FCSTD DOCUMENT  (FreeCAD 0.18.4R)
Label: container.v6
License: All rights reserved
LicenseURL: http://en.wikipedia.org/wiki/All_rights_reserved
objects: Part::Feature×11, Part::Extrusion×10, Part::Part2DObjectPython×7, Part::MultiFuse×3, Part::FeaturePython×3, App::DocumentObjectGroup×2, Part::Cut×1
note: 35 computed .brp shape members not serialized (recipe doc carries the construction recipe); baked Part::Feature solids carry a one-line shape summary decoded from their .brp

FEATURE [Part::Feature] Cut001001  label="Cut002"
  shape: bbox 73.48 x 120 x 121.6 mm, 4537 faces (baked)
FEATURE [Part::Feature] Fusion018002001008014
  Placement = pos=(63.0552,-240.375,-121.554) rot=(0,0,1;0rad)
  shape: bbox 46.3 x 120 x 5.151 mm, 1154 faces (baked)
FEATURE [Part::Part2DObjectPython] Wire  # Draft 2D object (typed FeaturePython)
  ChamferSize = 0
  Closed = true
  End = (149.94,5.9047,-131.382)
  FilletRadius = 0
  Length = 330.896
  MakeFace = true
  Placement = pos=(137.639,5.9047,-9.82831) rot=(1,0,0;1.5708rad)
  Points = (4) [(0,0,0),(-43.2967,-6.92779e-14,1.33227e-14),(-30.9437,-121.554,-2.04281e-14),(12.3006,-121.554,-1.59872e-14)]
  Start = (137.639,5.9047,-9.82831)
  Subdivisions = 0
  Support = -> [Cut001001]
FEATURE [Part::Extrusion] Extrusion
  Base = -> Wire
  Dir = (-2.55e-14,-117,3.6e-15)
  DirMode = 0
  FaceMakerClass = Part::FaceMakerBullseye
  LengthFwd = 0
  LengthRev = 0
  Solid = true
  Symmetric = false
FEATURE [Part::Cut] Cut
  Base = -> Cut001001
  Tool = -> Extrusion
FEATURE [Part::Feature] Fusion001002001  label="Fusion001003"
  shape: bbox 4.191 x 71 x 7.994 mm, 13 faces (baked)
FEATURE [Part::Feature] Face
  shape: bbox 0.8119 x 5 x 7.959 mm, 1 faces, 0 solids (baked)
FEATURE [Part::Extrusion] Extrusion001
  Base = -> Face
  Dir = (1.17358,-1.56e-14,0.119723)
  DirMode = 0
  FaceMakerClass = Part::FaceMakerBullseye
  LengthFwd = 0
  LengthRev = 0
  Solid = true
  Symmetric = false
FEATURE [Part::Feature] Face001
  shape: bbox 0.8119 x 6 x 7.959 mm, 1 faces, 0 solids (baked)
FEATURE [Part::Extrusion] Extrusion002
  Base = -> Face001
  Dir = (1.17358,-1.58e-14,0.119723)
  DirMode = 0
  FaceMakerClass = Part::FaceMakerBullseye
  LengthFwd = 0
  LengthRev = 0
  Solid = true
  Symmetric = false
FEATURE [Part::Feature] Fusion018002001008015
  Placement = pos=(6.06632,-6.985e-12,-59.6925) rot=(0,0,1;0rad)
  shape: bbox 4.191 x 71 x 7.994 mm, 13 faces (baked)
FEATURE [Part::Feature] Face002
  Placement = pos=(6.06632,-6.985e-12,-59.6925) rot=(0,0,1;0rad)
  shape: bbox 0.8119 x 6 x 7.959 mm, 1 faces, 0 solids (baked)
FEATURE [Part::Extrusion] Extrusion003
  Base = -> Face002
  Dir = (1.16236,-1.57e-14,0.118578)
  DirMode = 0
  FaceMakerClass = Part::FaceMakerBullseye
  LengthFwd = 0
  LengthRev = 0
  Solid = true
  Symmetric = false
FEATURE [Part::Feature] Face003
  Placement = pos=(6.06632,-6.985e-12,-59.6925) rot=(0,0,1;0rad)
  shape: bbox 0.8119 x 5 x 7.959 mm, 1 faces, 0 solids (baked)
FEATURE [Part::Extrusion] Extrusion004
  Base = -> Face003
  Dir = (1.16101,-1.54e-14,0.118441)
  DirMode = 0
  FaceMakerClass = Part::FaceMakerBullseye
  LengthFwd = 0
  LengthRev = 0
  Solid = true
  Symmetric = false
FEATURE [Part::Part2DObjectPython] Wire001  # Draft 2D object (typed FeaturePython)
  ChamferSize = 0
  Closed = true
  End = (147.812,-11.2487,-95.1691)
  FilletRadius = 0
  Length = 49.7972
  MakeFace = true
  Placement = pos=(148.52,-11.2487,-102.133) rot=(0,1,0;1.46952rad)
  Points = (8) [(0,0,0),(1.37849,-1.3786,0),(1.37849,-15.3786,0),(-4.26326e-14,-16.7572,0),(-6.99946,-16.7572,-2.84217e-13),(-8.37795,-15.3786,0),(-8.37795,-1.3786,0),(-6.99946,7.10543e-15,0)]
  Start = (148.52,-11.2487,-102.133)
  Subdivisions = 0
FEATURE [Part::Part2DObjectPython] Wire002  # Draft 2D object (typed FeaturePython)
  ChamferSize = 0
  Closed = true
  End = (141.767,-77.7487,-35.6862)
  FilletRadius = 0
  Length = 49.7972
  MakeFace = true
  Placement = pos=(142.475,-77.7487,-42.6498) rot=(0,1,0;1.46952rad)
  Points = (8) [(0,0,0),(1.37849,-1.3786,0),(1.37849,-15.3786,0),(-4.26326e-14,-16.7572,0),(-6.99946,-16.7572,-2.84217e-13),(-8.37795,-15.3786,0),(-8.37795,-1.3786,0),(-6.99946,0,1.7053e-13)]
  Start = (142.475,-77.7487,-42.6498)
  Subdivisions = 0
FEATURE [Part::Part2DObjectPython] Wire003  # Draft 2D object (typed FeaturePython)
  ChamferSize = 0
  Closed = true
  End = (147.812,-81.2487,-95.1691)
  FilletRadius = 0
  Length = 49.7972
  MakeFace = true
  Placement = pos=(148.52,-81.2487,-102.133) rot=(0,1,0;1.46952rad)
  Points = (8) [(0,0,0),(1.37849,-1.3786,0),(1.37849,-15.3786,0),(-4.26326e-14,-16.7572,0),(-6.99946,-16.7572,-2.84217e-13),(-8.37795,-15.3786,0),(-8.37795,-1.3786,0),(-6.99946,0,2.27374e-13)]
  Start = (148.52,-81.2487,-102.133)
  Subdivisions = 0
FEATURE [Part::Part2DObjectPython] Wire004  # Draft 2D object (typed FeaturePython)
  ChamferSize = 0
  Closed = true
  End = (141.767,-14.7487,-35.6862)
  FilletRadius = 0
  Length = 49.7972
  MakeFace = true
  Placement = pos=(142.475,-14.7487,-42.6498) rot=(0,1,0;1.46952rad)
  Points = (8) [(0,0,0),(1.37849,-1.3786,0),(1.37849,-15.3786,0),(-4.26326e-14,-16.7572,0),(-6.99946,-16.7572,-2.84217e-13),(-8.37795,-15.3786,0),(-8.37795,-1.3786,0),(-6.99946,7.10543e-15,0)]
  Start = (142.475,-14.7487,-42.6498)
  Subdivisions = 0
FEATURE [Part::Extrusion] Extrusion005
  Base = -> Wire004
  Dir = (-1.48467,5.8e-15,-0.150881)
  DirMode = 0
  FaceMakerClass = Part::FaceMakerBullseye
  LengthFwd = 0
  LengthRev = 0
  Solid = true
  Symmetric = false
FEATURE [Part::Extrusion] Extrusion006
  Base = -> Wire002
  Dir = (-1.48467,6.4e-15,-0.150881)
  DirMode = 0
  FaceMakerClass = Part::FaceMakerBullseye
  LengthFwd = 0
  LengthRev = 0
  Solid = true
  Symmetric = false
FEATURE [Part::Extrusion] Extrusion007
  Base = -> Wire003
  Dir = (-1.48467,8.6e-15,-0.150881)
  DirMode = 0
  FaceMakerClass = Part::FaceMakerBullseye
  LengthFwd = 0
  LengthRev = 0
  Solid = true
  Symmetric = false
FEATURE [Part::Extrusion] Extrusion008
  Base = -> Wire001
  Dir = (-1.48467,5.7e-15,-0.150881)
  DirMode = 0
  FaceMakerClass = Part::FaceMakerBullseye
  LengthFwd = 0
  LengthRev = 0
  Solid = true
  Symmetric = false
FEATURE [Part::MultiFuse] Fusion
  Shapes = -> [Extrusion007,Fusion018002001008015,Extrusion008,Extrusion006,Fusion001002001,Extrusion005]
FEATURE [Part::MultiFuse] Fusion018002001008016
  Shapes = -> [Fusion,Cut]
FEATURE [Part::Feature] Fusion018002001008016001  label="Fusion018002001008017"
  shape: bbox 73.48 x 120 x 121.6 mm, 4427 faces (baked)
FEATURE [Part::FeaturePython] Slice_child1  label="Slice.1"  # WARN: FeaturePython — macro-defined, semantics opaque (R4)
  FilterType = 1
  Invert = false
  OverrideMaxVal = 0
  WindowFrom = 80
  WindowTo = 100
  items = 1
FEATURE [App::DocumentObjectGroup] GrExplode_Slice  label="Exploded Slice"
  Group = -> [Slice_child1]
FEATURE [Part::Part2DObjectPython] Rectangle  # Draft 2D object (typed FeaturePython)
  ChamferSize = 0
  Columns = 1
  FilletRadius = 0
  Height = 193
  Length = 154
  MakeFace = true
  Placement = pos=(92.5503,-317.731,-183.654) rot=(1,0,0;3.14159rad)
  Rows = 1
  Support = -> [Slice_child1]
FEATURE [Part::FeaturePython] Slice  # WARN: FeaturePython — macro-defined, semantics opaque (R4)
  Base = -> Slice_child1
  Mode = 1
  Tolerance = 0
  Tools = -> [Rectangle]
FEATURE [Part::FeaturePython] Slice_child0  label="Slice.0"  # WARN: FeaturePython — macro-defined, semantics opaque (R4)
  Base = -> Slice
  FilterType = 1
  Invert = false
  OverrideMaxVal = 0
  Placement = pos=(258.315,131.738,-193.634) rot=(0,1,0;3.14159rad)
  WindowFrom = 80
  WindowTo = 100
  items = 0
FEATURE [Part::Part2DObjectPython] Wire005  # Draft 2D object (typed FeaturePython)
  ChamferSize = 0
  Closed = true
  End = (151.417,-340.152,-131.382)
  FilletRadius = 0
  Length = 8.77005
  MakeFace = true
  Placement = pos=(151.72,-340.152,-128.398) rot=(0.787614,0.60907,-0.093265;3.93915rad)
  Points = (3) [(0,0,0),(-1.74661,0.247326,3.33188),(-1.0363,1.74338,2.21059)]
  Start = (151.72,-340.152,-128.398)
  Subdivisions = 0
FEATURE [Part::Extrusion] Extrusion009
  Base = -> Wire005
  Dir = (2.78485e-11,115.318,-5.34519e-10)
  DirMode = 0
  FaceMakerClass = Part::FaceMakerBullseye
  LengthFwd = 0
  LengthRev = 0
  Solid = true
  Symmetric = false
FEATURE [Part::MultiFuse] Fusion018002001008016002
  Shapes = -> [Extrusion009,Slice_child0]
FEATURE [App::DocumentObjectGroup] GrExplode_Slice001  label="Exploded Slice001"
  Group = -> [Fusion018002001008016002]
FEATURE [Part::Feature] Fusion018002001008016002_solid  label="Fusion018002001008016002 (Solid)"
  shape: bbox 73.97 x 118.7 x 121.4 mm, 508 faces (baked)
FEATURE [Part::Feature] Fusion018002001008016003
  Placement = pos=(52.9375,-470.393,-121.554) rot=(0,0,1;0rad)
  shape: bbox 46.3 x 120 x 5.151 mm, 1154 faces (baked)
